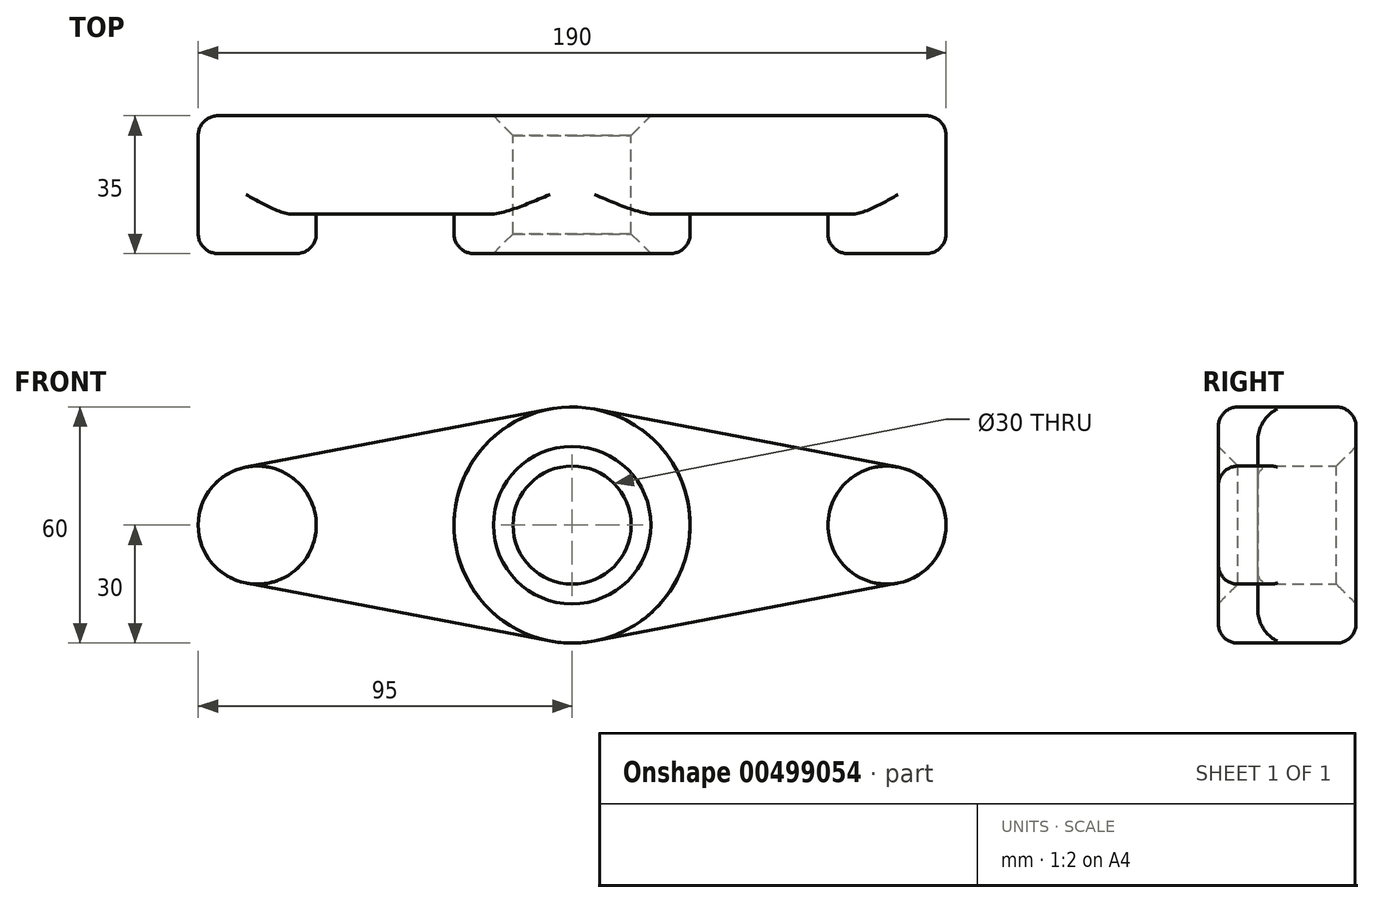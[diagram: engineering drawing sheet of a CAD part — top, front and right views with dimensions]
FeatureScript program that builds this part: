
annotation { "Feature Type Name" : "Feature", "Feature Type Description" : "" }
export const myFeature = defineFeature(function(context is Context, id is Id, definition is map)
    precondition{}
    {
        {
            var Q0;
            Q0=qCreatedBy(makeId("Front.planeOp"),FACE);
            var sketch = newSketch(context, id + "F0", { "sketchPlane" : qUnion([Q0])});
            skCircle(sketch, "E0", {"center": v(0, 0) * mm, "radius": 30 * mm});
            skCircle(sketch, "E1", {"center": v(0, 0) * mm, "radius": 15 * mm});
            skCircle(sketch, "E2", {"center": v(80, 0) * mm, "radius": 15 * mm});
            skCircle(sketch, "E3", {"center": v(-80, 0) * mm, "radius": 15 * mm});
            skLineSegment(sketch, "E4", {"start": v(-82.81, 14.73) * mm, "end": v(-5.62, 29.47) * mm});
            skLineSegment(sketch, "E5", {"start": v(82.81, -14.73) * mm, "end": v(5.62, -29.47) * mm});
            skLineSegment(sketch, "E6", {"start": v(-5.62, -29.47) * mm, "end": v(-82.81, -14.73) * mm});
            skLineSegment(sketch, "E7", {"start": v(5.63, 29.47) * mm, "end": v(82.81, 14.73) * mm});
            skSolve(sketch);
        }
        {
            var Q0;
            {var subQ0=sQuery(id+"F0.wireOp",EDGE,"E3");var subQ1=makeQuery(id+"F0.imprint","INTERSECT",VERTEX,{"derivedFrom":[subQ0,sQuery(id+"F0.wireOp",EDGE,"E4")]});Q0=makeQuery(id+"F0.imprint","IMPRINT",FACE,{"disambiguationData":[TD([[makeQuery(id+"F0.imprint","IMPRINT",EDGE,{"disambiguationData":[TD([[subQ1,-1.0]])],"derivedFrom":subQ0}),1.0]])]});}
            var Q1;
            {var subQ0=sQuery(id+"F0.wireOp",EDGE,"E4");Q1=makeQuery(id+"F0.imprint","IMPRINT",FACE,{"disambiguationData":[TD([[makeQuery(id+"F0.imprint","IMPRINT",EDGE,{"derivedFrom":subQ0}),-1.0]])]});}
            var Q2;
            Q2=makeQuery(id+"F0.imprint","IMPRINT",FACE,{"disambiguationData":[TD([[makeQuery(id+"F0.imprint","IMPRINT",EDGE,{"derivedFrom":sQuery(id+"F0.wireOp",EDGE,"E1")}),-1.0]])]});
            var Q3;
            {var subQ0=sQuery(id+"F0.wireOp",EDGE,"E5");Q3=makeQuery(id+"F0.imprint","IMPRINT",FACE,{"disambiguationData":[TD([[makeQuery(id+"F0.imprint","IMPRINT",EDGE,{"derivedFrom":subQ0}),-1.0]])]});}
            var Q4;
            {var subQ0=sQuery(id+"F0.wireOp",EDGE,"E2");var subQ1=makeQuery(id+"F0.imprint","INTERSECT",VERTEX,{"derivedFrom":[subQ0,sQuery(id+"F0.wireOp",EDGE,"E5")]});Q4=makeQuery(id+"F0.imprint","IMPRINT",FACE,{"disambiguationData":[TD([[makeQuery(id+"F0.imprint","IMPRINT",EDGE,{"disambiguationData":[TD([[subQ1,1.0]])],"derivedFrom":subQ0}),1.0]])]});}
            extrude(context, id + "F1", {"entities" : qUnion([Q0, Q1, Q2, Q3, Q4]), "depth" : 25 * mm});
        }
        {
            var Q0;
            {var subQ0=sQuery(id+"F0.wireOp",EDGE,"E3");var subQ1=makeQuery(id+"F0.imprint","INTERSECT",VERTEX,{"derivedFrom":[subQ0,sQuery(id+"F0.wireOp",EDGE,"E4")]});Q0=makeQuery(id+"F0.imprint","IMPRINT",FACE,{"disambiguationData":[TD([[makeQuery(id+"F0.imprint","IMPRINT",EDGE,{"disambiguationData":[TD([[subQ1,-1.0]])],"derivedFrom":subQ0}),1.0]])]});}
            var Q1;
            Q1=makeQuery(id+"F0.imprint","IMPRINT",FACE,{"disambiguationData":[TD([[makeQuery(id+"F0.imprint","IMPRINT",EDGE,{"derivedFrom":sQuery(id+"F0.wireOp",EDGE,"E1")}),-1.0]])]});
            var Q2;
            {var subQ0=sQuery(id+"F0.wireOp",EDGE,"E2");var subQ1=makeQuery(id+"F0.imprint","INTERSECT",VERTEX,{"derivedFrom":[subQ0,sQuery(id+"F0.wireOp",EDGE,"E5")]});Q2=makeQuery(id+"F0.imprint","IMPRINT",FACE,{"disambiguationData":[TD([[makeQuery(id+"F0.imprint","IMPRINT",EDGE,{"disambiguationData":[TD([[subQ1,1.0]])],"derivedFrom":subQ0}),1.0]])]});}
            extrude(context, id + "F2", {"entities" : qUnion([Q0, Q1, Q2]), "operationType" : NewBodyOperationType.ADD, "depth" : 35 * mm});
        }
        {
            var Q0;
            Q0=makeQuery(id+"F2.opExtrude","CAP_EDGE",EDGE,{"disambiguationData":[OSD([sQuery(id+"F0.wireOp",EDGE,"E1")])],"isStart":false});
            var Q1;
            Q1=makeQuery(id+"F1.opExtrude","CAP_EDGE",EDGE,{"disambiguationData":[OSD([sQuery(id+"F0.wireOp",EDGE,"E1")])],"isStart":true});
            chamfer(context, id + "F3", {"entities" : qUnion([Q0, Q1]), "width" : 5 * mm, "tangentPropagation" : true});
        }
        {
            var Q0;
            Q0=makeQuery(id+"F2.opExtrude","CAP_EDGE",EDGE,{"disambiguationData":[OSD([sQuery(id+"F0.wireOp",EDGE,"E3")])],"isStart":false});
            var Q1;
            Q1=makeQuery(id+"F2.opExtrude","CAP_EDGE",EDGE,{"disambiguationData":[OSD([sQuery(id+"F0.wireOp",EDGE,"E2")])],"isStart":false});
            var Q2;
            Q2=makeQuery(id+"F1.opExtrude","CAP_EDGE",EDGE,{"disambiguationData":[OSD([sQuery(id+"F0.wireOp",EDGE,"E5")])],"isStart":true});
            var Q3;
            Q3=makeQuery(id+"F2.opExtrude","CAP_EDGE",EDGE,{"disambiguationData":[OSD([sQuery(id+"F0.wireOp",EDGE,"E0")])],"isStart":false});
            var Q4;
            Q4=makeQuery(id+"F1.opExtrude","CAP_EDGE",EDGE,{"disambiguationData":[OSD([sQuery(id+"F0.wireOp",EDGE,"E6")])],"isStart":false});
            var Q5;
            Q5=makeQuery(id+"F1.opExtrude","CAP_EDGE",EDGE,{"disambiguationData":[OSD([sQuery(id+"F0.wireOp",EDGE,"E4")])],"isStart":false});
            var Q6;
            Q6=makeQuery(id+"F1.opExtrude","CAP_EDGE",EDGE,{"disambiguationData":[OSD([sQuery(id+"F0.wireOp",EDGE,"E7")])],"isStart":false});
            var Q7;
            Q7=makeQuery(id+"F1.opExtrude","CAP_EDGE",EDGE,{"disambiguationData":[OSD([sQuery(id+"F0.wireOp",EDGE,"E5")])],"isStart":false});
            fillet(context, id + "F4", {"entities" : qUnion([Q0, Q1, Q2, Q3, Q4, Q5, Q6, Q7]), "radius" : 5 * mm, "tangentPropagation" : true, "allowEdgeOverflow" : false});
        }
    });
